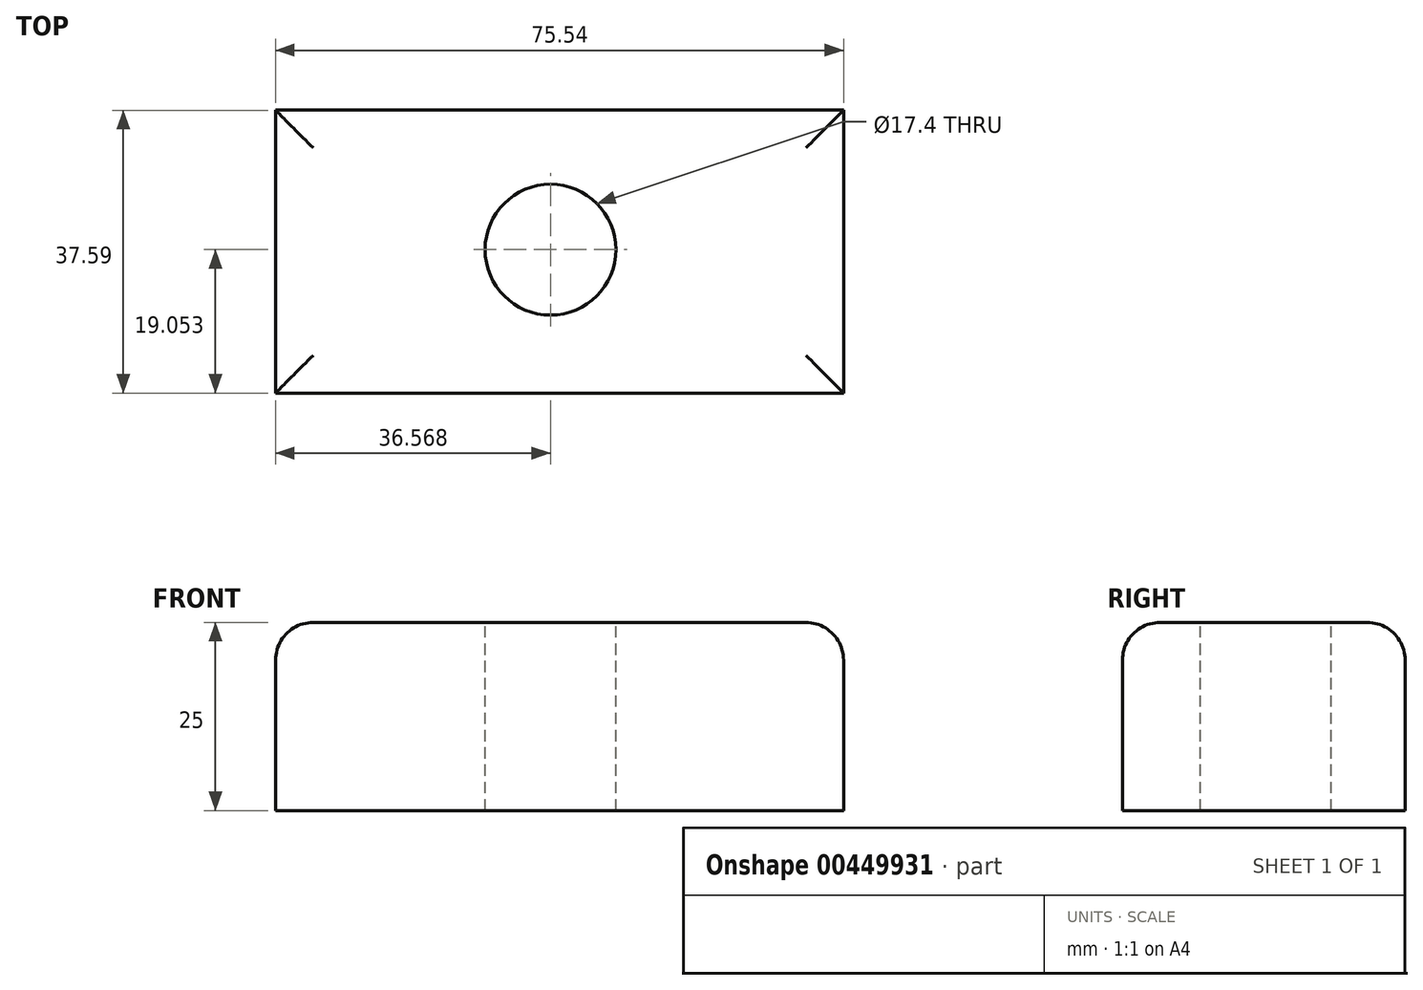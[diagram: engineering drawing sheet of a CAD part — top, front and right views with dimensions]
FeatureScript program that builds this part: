
annotation { "Feature Type Name" : "Feature", "Feature Type Description" : "" }
export const myFeature = defineFeature(function(context is Context, id is Id, definition is map)
    precondition{}
    {
        {
            var Q0;
            Q0=qCreatedBy(makeId("Top.planeOp"),FACE);
            var sketch = newSketch(context, id + "F0", { "sketchPlane" : qUnion([Q0])});
            skLineSegment(sketch, "E0", {"start": v(-60.84, 37.6) * mm, "end": v(14.7, 37.6) * mm});
            skLineSegment(sketch, "E1", {"start": v(14.7, 37.6) * mm, "end": v(14.7, 0) * mm});
            skLineSegment(sketch, "E2", {"start": v(14.7, 0) * mm, "end": v(-60.84, 0) * mm});
            skLineSegment(sketch, "E3", {"start": v(-60.84, 0) * mm, "end": v(-60.84, 37.6) * mm});
            skSolve(sketch);
        }
        {
            var Q0;
            Q0=makeQuery(id+"F0.imprint","IMPRINT",FACE,{"disambiguationData":[TD([[makeQuery(id+"F0.imprint","IMPRINT",EDGE,{"derivedFrom":sQuery(id+"F0.wireOp",EDGE,"E0")}),-1.0]])]});
            extrude(context, id + "F1", {"entities" : qUnion([Q0]), "depth" : 25 * mm});
        }
        {
            var Q0;
            Q0=makeQuery(id+"F1.opExtrude","CAP_EDGE",EDGE,{"disambiguationData":[OSD([sQuery(id+"F0.wireOp",EDGE,"E2")])],"isStart":false});
            var Q1;
            Q1=makeQuery(id+"F1.opExtrude","CAP_EDGE",EDGE,{"disambiguationData":[OSD([sQuery(id+"F0.wireOp",EDGE,"E3")])],"isStart":false});
            var Q2;
            Q2=makeQuery(id+"F1.opExtrude","CAP_EDGE",EDGE,{"disambiguationData":[OSD([sQuery(id+"F0.wireOp",EDGE,"E0")])],"isStart":false});
            var Q3;
            Q3=makeQuery(id+"F1.opExtrude","CAP_EDGE",EDGE,{"disambiguationData":[OSD([sQuery(id+"F0.wireOp",EDGE,"E1")])],"isStart":false});
            fillet(context, id + "F2", {"entities" : qUnion([Q0, Q1, Q2, Q3]), "radius" : 5 * mm, "tangentPropagation" : true, "allowEdgeOverflow" : false});
        }
        {
            var Q0;
            Q0=makeQuery(id+"F1.opExtrude","CAP_FACE",FACE,{"disambiguationData":[OSD([sQuery(id+"F0.wireOp",EDGE,"E0"),sQuery(id+"F0.wireOp",EDGE,"E1"),sQuery(id+"F0.wireOp",EDGE,"E2"),sQuery(id+"F0.wireOp",EDGE,"E3")])],"isStart":false});
            var sketch = newSketch(context, id + "F3", { "sketchPlane" : qUnion([Q0])});
            skCircle(sketch, "E4", {"center": v(-24.27, 19.05) * mm, "radius": 8.7 * mm});
            skSolve(sketch);
        }
        {
            var Q0;
            Q0=makeQuery(id+"F3.imprint","IMPRINT",FACE,{"disambiguationData":[TD([[makeQuery(id+"F3.imprint","IMPRINT",EDGE,{"derivedFrom":sQuery(id+"F3.wireOp",EDGE,"E4")}),1.0]])]});
            extrude(context, id + "F4", {"entities" : qUnion([Q0]), "operationType" : NewBodyOperationType.REMOVE, "oppositeDirection" : true, "depth" : 25 * mm});
        }
    });
